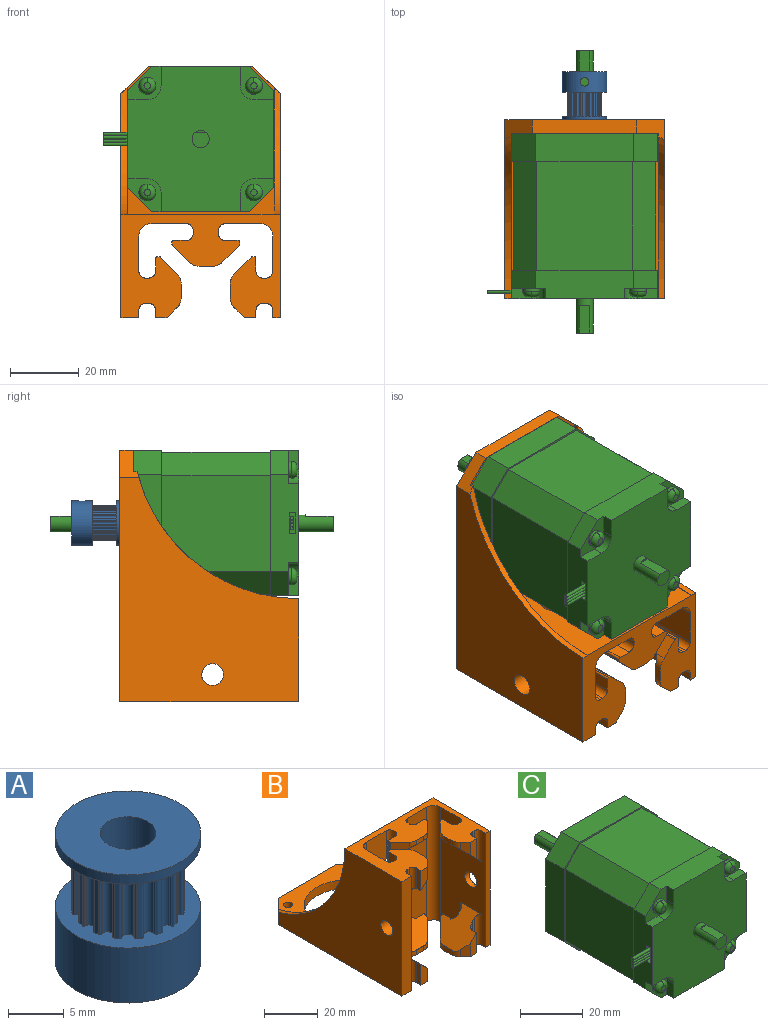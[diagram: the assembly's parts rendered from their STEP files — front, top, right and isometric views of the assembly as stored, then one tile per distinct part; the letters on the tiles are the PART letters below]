
ASSEMBLY  parts=3 mates=2
PART A: 104 faces, bbox 13x13x14 mm
  f0: cylinder r=2.5mm len=14mm, axis (0,0,1), area 214.8mm2, adj f2,f102,f103
  f1: cylinder r=6.5mm len=13mm, axis (0,0,1), area 240.1mm2, adj f2,f3,f103
  f2: plane 13x13mm, normal (0,0,-1), area 113.1mm2, adj f0,f1
  f3: plane 13x13mm, normal (0,0,1), area 62.7mm2, adj f1,f4,f5,f6,f7,f8,f9,f10
  f4: cylinder r=0.15mm len=7mm, axis (0,0,-1), area 1.7mm2, adj f3,f5,f99,f100
  f5: cylinder r=1mm len=7mm, axis (0,0,-1), area 1.7mm2, adj f3,f4,f6,f100
  f6: cylinder r=0.56mm len=7mm, axis (0,0,-1), area 9mm2, adj f3,f5,f7,f100
  f7: cylinder r=1mm len=7mm, axis (0,0,-1), area 1.7mm2, adj f3,f6,f8,f100
  f8: cylinder r=0.15mm len=7mm, axis (0,0,-1), area 1.7mm2, adj f3,f7,f9,f100
  f9: plane 7x0.49mm, normal (0.98,0.2,0), area 3.5mm2, adj f3,f8,f10,f100
  f10: cylinder r=0.15mm len=7mm, axis (0,0,-1), area 1.7mm2, adj f3,f9,f11,f100
  f11: cylinder r=1mm len=7mm, axis (0,0,-1), area 1.7mm2, adj f3,f10,f12,f100
  f12: cylinder r=0.56mm len=7mm, axis (0,0,-1), area 9mm2, adj f3,f11,f13,f100
  f13: cylinder r=1mm len=7mm, axis (0,0,-1), area 1.7mm2, adj f3,f12,f14,f100
  f14: cylinder r=0.15mm len=7mm, axis (0,0,-1), area 1.7mm2, adj f3,f13,f15,f100
  f15: plane 7x0.41mm, normal (0.83,0.56,0), area 3.5mm2, adj f3,f14,f16,f100
  f16: cylinder r=0.15mm len=7mm, axis (0,0,-1), area 1.7mm2, adj f3,f15,f17,f100
  f17: cylinder r=1mm len=7mm, axis (0,0,-1), area 1.7mm2, adj f3,f16,f18,f100
  f18: cylinder r=0.56mm len=7mm, axis (0,0,-1), area 9mm2, adj f3,f17,f19,f100
  f19: cylinder r=1mm len=7mm, axis (0,0,-1), area 1.7mm2, adj f3,f18,f20,f100
  f20: cylinder r=0.15mm len=7mm, axis (0,0,-1), area 1.7mm2, adj f3,f19,f21,f100
  f21: plane 7x0.41mm, normal (0.56,0.83,0), area 3.5mm2, adj f3,f20,f22,f100
  f22: cylinder r=0.15mm len=7mm, axis (0,0,-1), area 1.7mm2, adj f3,f21,f23,f100
  f23: cylinder r=1mm len=7mm, axis (0,0,-1), area 1.7mm2, adj f3,f22,f24,f100
  f24: cylinder r=0.56mm len=7mm, axis (0,0,-1), area 9mm2, adj f3,f23,f25,f100
  f25: cylinder r=1mm len=7mm, axis (0,0,-1), area 1.7mm2, adj f3,f24,f26,f100
  f26: cylinder r=0.15mm len=7mm, axis (0,0,-1), area 1.7mm2, adj f3,f25,f27,f100
  f27: plane 7x0.49mm, normal (0.2,0.98,0), area 3.5mm2, adj f3,f26,f28,f100
  f28: cylinder r=0.15mm len=7mm, axis (0,0,-1), area 1.7mm2, adj f3,f27,f29,f100
  f29: cylinder r=1mm len=7mm, axis (0,0,-1), area 1.7mm2, adj f3,f28,f30,f100
  f30: cylinder r=0.56mm len=7mm, axis (0,0,-1), area 9mm2, adj f3,f29,f31,f100
  f31: cylinder r=1mm len=7mm, axis (0,0,-1), area 1.7mm2, adj f3,f30,f32,f100
  f32: cylinder r=0.15mm len=7mm, axis (0,0,-1), area 1.7mm2, adj f3,f31,f33,f100
  f33: plane 7x0.49mm, normal (-0.2,0.98,0), area 3.5mm2, adj f3,f32,f34,f100
  f34: cylinder r=0.15mm len=7mm, axis (0,0,-1), area 1.7mm2, adj f3,f33,f35,f100
  f35: cylinder r=1mm len=7mm, axis (0,0,-1), area 1.7mm2, adj f3,f34,f36,f100
  f36: cylinder r=0.56mm len=7mm, axis (0,0,-1), area 9mm2, adj f3,f35,f37,f100
  f37: cylinder r=1mm len=7mm, axis (0,0,-1), area 1.7mm2, adj f3,f36,f38,f100
  f38: cylinder r=0.15mm len=7mm, axis (0,0,-1), area 1.7mm2, adj f3,f37,f39,f100
  f39: plane 7x0.41mm, normal (-0.56,0.83,0), area 3.5mm2, adj f3,f38,f40,f100
  f40: cylinder r=0.15mm len=7mm, axis (0,0,-1), area 1.7mm2, adj f3,f39,f41,f100
  f41: cylinder r=1mm len=7mm, axis (0,0,-1), area 1.7mm2, adj f3,f40,f42,f100
  f42: cylinder r=0.56mm len=7mm, axis (0,0,-1), area 9mm2, adj f3,f41,f43,f100
  f43: cylinder r=1mm len=7mm, axis (0,0,-1), area 1.7mm2, adj f3,f42,f44,f100
  f44: cylinder r=0.15mm len=7mm, axis (0,0,-1), area 1.7mm2, adj f3,f43,f45,f100
  f45: plane 7x0.41mm, normal (-0.83,0.56,0), area 3.5mm2, adj f3,f44,f46,f100
  f46: cylinder r=0.15mm len=7mm, axis (0,0,-1), area 1.7mm2, adj f3,f45,f47,f100
  f47: cylinder r=1mm len=7mm, axis (0,0,-1), area 1.7mm2, adj f3,f46,f48,f100
  f48: cylinder r=0.56mm len=7mm, axis (0,0,-1), area 9mm2, adj f3,f47,f49,f100
  f49: cylinder r=1mm len=7mm, axis (0,0,-1), area 1.7mm2, adj f3,f48,f50,f100
  f50: cylinder r=0.15mm len=7mm, axis (0,0,-1), area 1.7mm2, adj f3,f49,f51,f100
  f51: plane 7x0.49mm, normal (-0.98,0.2,0), area 3.5mm2, adj f3,f50,f52,f100
  f52: cylinder r=0.15mm len=7mm, axis (0,0,-1), area 1.7mm2, adj f3,f51,f53,f100
  f53: cylinder r=1mm len=7mm, axis (0,0,-1), area 1.7mm2, adj f3,f52,f54,f100
  f54: cylinder r=0.56mm len=7mm, axis (0,0,-1), area 9mm2, adj f3,f53,f55,f100
  f55: cylinder r=1mm len=7mm, axis (0,0,-1), area 1.7mm2, adj f3,f54,f56,f100
  f56: cylinder r=0.15mm len=7mm, axis (0,0,-1), area 1.7mm2, adj f3,f55,f57,f100
  f57: plane 7x0.49mm, normal (-0.98,-0.2,0), area 3.5mm2, adj f3,f56,f58,f100
  f58: cylinder r=0.15mm len=7mm, axis (0,0,-1), area 1.7mm2, adj f3,f57,f59,f100
  f59: cylinder r=1mm len=7mm, axis (0,0,-1), area 1.7mm2, adj f3,f58,f60,f100
  f60: cylinder r=0.56mm len=7mm, axis (0,0,-1), area 9mm2, adj f3,f59,f61,f100
  f61: cylinder r=1mm len=7mm, axis (0,0,-1), area 1.7mm2, adj f3,f60,f62,f100
  f62: cylinder r=0.15mm len=7mm, axis (0,0,-1), area 1.7mm2, adj f3,f61,f63,f100
  f63: plane 7x0.41mm, normal (-0.83,-0.56,0), area 3.5mm2, adj f3,f62,f64,f100
  f64: cylinder r=0.15mm len=7mm, axis (0,0,-1), area 1.7mm2, adj f3,f63,f65,f100
  f65: cylinder r=1mm len=7mm, axis (0,0,-1), area 1.7mm2, adj f3,f64,f66,f100
  f66: cylinder r=0.56mm len=7mm, axis (0,0,-1), area 9mm2, adj f3,f65,f67,f100
  f67: cylinder r=1mm len=7mm, axis (0,0,-1), area 1.7mm2, adj f3,f66,f68,f100
  f68: cylinder r=0.15mm len=7mm, axis (0,0,-1), area 1.7mm2, adj f3,f67,f69,f100
  f69: plane 7x0.41mm, normal (-0.56,-0.83,0), area 3.5mm2, adj f3,f68,f70,f100
  f70: cylinder r=0.15mm len=7mm, axis (0,0,-1), area 1.7mm2, adj f3,f69,f71,f100
  f71: cylinder r=1mm len=7mm, axis (0,0,-1), area 1.7mm2, adj f3,f70,f72,f100
  f72: cylinder r=0.56mm len=7mm, axis (0,0,-1), area 9mm2, adj f3,f71,f73,f100
  f73: cylinder r=1mm len=7mm, axis (0,0,-1), area 1.7mm2, adj f3,f72,f74,f100
  f74: cylinder r=0.15mm len=7mm, axis (0,0,-1), area 1.7mm2, adj f3,f73,f75,f100
  f75: plane 7x0.49mm, normal (-0.2,-0.98,0), area 3.5mm2, adj f3,f74,f76,f100
  f76: cylinder r=0.15mm len=7mm, axis (0,0,-1), area 1.7mm2, adj f3,f75,f77,f100
  f77: cylinder r=1mm len=7mm, axis (0,0,-1), area 1.7mm2, adj f3,f76,f78,f100
  f78: cylinder r=0.56mm len=7mm, axis (0,0,-1), area 9mm2, adj f3,f77,f79,f100
  f79: cylinder r=1mm len=7mm, axis (0,0,-1), area 1.7mm2, adj f3,f78,f80,f100
  f80: cylinder r=0.15mm len=7mm, axis (0,0,-1), area 1.7mm2, adj f3,f79,f81,f100
  f81: plane 7x0.49mm, normal (0.2,-0.98,0), area 3.5mm2, adj f3,f80,f82,f100
  f82: cylinder r=0.15mm len=7mm, axis (0,0,-1), area 1.7mm2, adj f3,f81,f83,f100
  f83: cylinder r=1mm len=7mm, axis (0,0,-1), area 1.7mm2, adj f3,f82,f84,f100
  f84: cylinder r=0.56mm len=7mm, axis (0,0,-1), area 9mm2, adj f3,f83,f85,f100
  f85: cylinder r=1mm len=7mm, axis (0,0,-1), area 1.7mm2, adj f3,f84,f86,f100
  f86: cylinder r=0.15mm len=7mm, axis (0,0,-1), area 1.7mm2, adj f3,f85,f87,f100
  f87: plane 7x0.41mm, normal (0.56,-0.83,0), area 3.5mm2, adj f3,f86,f88,f100
  f88: cylinder r=0.15mm len=7mm, axis (0,0,-1), area 1.7mm2, adj f3,f87,f89,f100
  f89: cylinder r=1mm len=7mm, axis (0,0,-1), area 1.7mm2, adj f3,f88,f90,f100
  f90: cylinder r=0.56mm len=7mm, axis (0,0,-1), area 9mm2, adj f3,f89,f91,f100
  f91: cylinder r=1mm len=7mm, axis (0,0,-1), area 1.7mm2, adj f3,f90,f92,f100
  f92: cylinder r=0.15mm len=7mm, axis (0,0,-1), area 1.7mm2, adj f3,f91,f93,f100
  f93: plane 7x0.41mm, normal (0.83,-0.56,0), area 3.5mm2, adj f3,f92,f94,f100
  f94: cylinder r=0.15mm len=7mm, axis (0,0,-1), area 1.7mm2, adj f3,f93,f95,f100
  f95: cylinder r=1mm len=7mm, axis (0,0,-1), area 1.7mm2, adj f3,f94,f96,f100
  f96: cylinder r=0.56mm len=7mm, axis (0,0,-1), area 9mm2, adj f3,f95,f97,f100
  f97: cylinder r=1mm len=7mm, axis (0,0,-1), area 1.7mm2, adj f3,f96,f98,f100
  f98: cylinder r=0.15mm len=7mm, axis (0,0,-1), area 1.7mm2, adj f3,f97,f99,f100
  f99: plane 7x0.49mm, normal (0.98,-0.2,0), area 3.5mm2, adj f3,f4,f98,f100
  f100: plane 13x13mm, normal (0,0,-1), area 62.7mm2, adj f4,f5,f6,f7,f8,f9,f10,f11
  f101: cylinder r=6.5mm len=13mm, axis (0,0,-1), area 40.8mm2, adj f100,f102
  f102: plane 13x13mm, normal (0,0,1), area 113.1mm2, adj f0,f101
  f103: cylinder r=1.25mm len=4.34mm, axis (0,-1,0), area 32.2mm2, adj f0,f1
PART B: 154 faces, bbox 46.4x73.1x52.1 mm
  f0: plane 52x10.23mm, normal (0,-1,0), area 397.5mm2, adj f41,f42,f43,f111,f125,f144,f145,f148
  f1: plane 9.14x3.34mm, normal (0,-1,0), area 24.9mm2, adj f91,f101,f111,f137
  f2: plane 9.14x3.34mm, normal (0,-1,0), area 24.9mm2, adj f92,f102,f125,f139
  f3: plane 9.14x3.34mm, normal (0,-1,0), area 24.9mm2, adj f89,f99,f111,f136
  f4: plane 9.14x3.34mm, normal (0,-1,0), area 24.9mm2, adj f90,f100,f125,f141
  f5: cylinder r=1.95mm len=14mm, axis (0,0,-1), area 40.8mm2, adj f7,f111,f117,f138
  f6: cylinder r=1.95mm len=14mm, axis (0,0,-1), area 40.8mm2, adj f8,f117,f125,f140
  f7: plane 12.05x0.96mm, normal (1,0,0), area 11.1mm2, adj f5,f9,f111,f138
  f8: plane 12.05x0.96mm, normal (1,0,0), area 11.1mm2, adj f6,f10,f125,f140
  f9: cylinder r=1.95mm len=11.09mm, axis (0,0,-1), area 30.2mm2, adj f7,f11,f111,f138
  f10: cylinder r=1.95mm len=11.09mm, axis (0,0,-1), area 30.2mm2, adj f8,f12,f125,f140
  f11: plane 9.14x3.77mm, normal (0,1,0), area 34.4mm2, adj f9,f13,f111,f138
  f12: plane 9.14x3.77mm, normal (0,1,0), area 34.4mm2, adj f10,f14,f125,f140
  f13: cylinder r=0.5mm len=9.14mm, axis (0,0,-1), area 7.1mm2, adj f11,f15,f111,f138
  f14: cylinder r=0.5mm len=9.14mm, axis (0,0,-1), area 7.1mm2, adj f12,f16,f125,f140
  f15: plane 8.63x0.53mm, normal (1,0,0), area 4.5mm2, adj f13,f17,f111,f138
  f16: plane 8.63x0.53mm, normal (1,0,0), area 4.5mm2, adj f14,f18,f125,f140
  f17: cylinder r=0.5mm len=8.1mm, axis (0,0,-1), area 3.1mm2, adj f15,f19,f111,f138
  f18: cylinder r=0.5mm len=8.1mm, axis (0,0,-1), area 3.1mm2, adj f16,f20,f125,f140
  f19: plane 7.75x5.05mm, normal (0.71,-0.71,0), area 37.3mm2, adj f17,f21,f111,f138
  f20: plane 7.75x5.05mm, normal (0.71,-0.71,0), area 37.3mm2, adj f18,f22,f125,f140
  f21: cylinder r=4.36mm len=2.78mm, axis (0,0,-1), area 6.5mm2, adj f19,f23,f111,f134,f138
  f22: cylinder r=4.36mm len=2.78mm, axis (0,0,-1), area 6.5mm2, adj f20,f24,f125,f135,f140
  f23: plane 3.8x2mm, normal (0,-1,0), area 7.6mm2, adj f21,f25,f111,f134
  f24: plane 3.8x2mm, normal (0,-1,0), area 7.6mm2, adj f22,f26,f125,f135
  f25: cylinder r=4.36mm len=2.78mm, axis (0,0,-1), area 6.5mm2, adj f23,f27,f111,f134,f138
  f26: cylinder r=4.36mm len=2.78mm, axis (0,0,-1), area 6.5mm2, adj f24,f28,f125,f135,f140
  f27: plane 7.75x5.05mm, normal (-0.71,-0.71,0), area 37.3mm2, adj f25,f29,f111,f138
  f28: plane 7.75x5.05mm, normal (-0.71,-0.71,0), area 37.3mm2, adj f26,f30,f125,f140
  f29: cylinder r=0.5mm len=8.1mm, axis (0,0,-1), area 3.1mm2, adj f27,f31,f111,f138
  f30: cylinder r=0.5mm len=8.1mm, axis (0,0,-1), area 3.1mm2, adj f28,f32,f125,f140
  f31: plane 8.63x0.53mm, normal (-1,0,0), area 4.5mm2, adj f29,f33,f111,f138
  f32: plane 8.63x0.53mm, normal (-1,0,0), area 4.5mm2, adj f30,f34,f125,f140
  f33: cylinder r=0.5mm len=9.14mm, axis (0,0,-1), area 7.1mm2, adj f31,f35,f111,f138
  f34: cylinder r=0.5mm len=9.14mm, axis (0,0,-1), area 7.1mm2, adj f32,f36,f125,f140
  f35: plane 9.14x3.77mm, normal (0,1,0), area 34.4mm2, adj f33,f37,f111,f138
  f36: plane 9.14x3.77mm, normal (0,1,0), area 34.4mm2, adj f34,f38,f125,f140
  f37: cylinder r=1.95mm len=11.09mm, axis (0,0,-1), area 30.2mm2, adj f35,f39,f111,f138
  f38: cylinder r=1.95mm len=11.09mm, axis (0,0,-1), area 30.2mm2, adj f36,f40,f125,f140
  f39: plane 12.05x0.96mm, normal (-1,0,0), area 11.1mm2, adj f37,f41,f111,f138
  f40: plane 11.18x0.96mm, normal (-1,0,0), area 10.7mm2, adj f38,f42,f125,f140,f149
  f41: cylinder r=1.95mm len=13.8mm, axis (0,0,-1), area 38.8mm2, adj f0,f39,f111,f138,f144,f151
  f42: cylinder r=1.95mm len=12.8mm, axis (0,0,-1), area 35.8mm2, adj f0,f40,f125,f145,f149
  f43: cylinder r=3.49mm len=52mm, axis (0,0,-1), area 296.8mm2, adj f0,f111,f118,f125
  f44: cylinder r=1.95mm len=14mm, axis (0,0,-1), area 40.8mm2, adj f46,f111,f118,f136
  f45: cylinder r=1.95mm len=14mm, axis (0,0,-1), area 40.8mm2, adj f47,f118,f125,f141
  f46: plane 12.05x0.96mm, normal (0,1,0), area 11.1mm2, adj f44,f48,f111,f136
  f47: plane 12.05x0.96mm, normal (0,1,0), area 11.1mm2, adj f45,f49,f125,f141
  f48: cylinder r=1.95mm len=11.09mm, axis (0,0,-1), area 30.2mm2, adj f46,f50,f111,f136
  f49: cylinder r=1.95mm len=11.09mm, axis (0,0,-1), area 30.2mm2, adj f47,f51,f125,f141
  f50: plane 9.14x3.77mm, normal (-1,0,0), area 34.4mm2, adj f48,f52,f111,f136
  f51: plane 9.14x3.77mm, normal (-1,0,0), area 34.4mm2, adj f49,f53,f125,f141
  f52: cylinder r=0.5mm len=9.14mm, axis (0,0,-1), area 7.1mm2, adj f50,f54,f111,f136
  f53: cylinder r=0.5mm len=9.14mm, axis (0,0,-1), area 7.1mm2, adj f51,f55,f125,f141
  f54: plane 8.63x0.57mm, normal (0,1,0), area 4.7mm2, adj f52,f56,f111,f136
  f55: plane 8.63x0.57mm, normal (0,1,0), area 4.7mm2, adj f53,f57,f125,f141
  f56: cylinder r=0.5mm len=8.07mm, axis (0,0,-1), area 3.1mm2, adj f54,f58,f111,f136
  f57: cylinder r=0.5mm len=8.07mm, axis (0,0,-1), area 3.1mm2, adj f55,f59,f125,f141
  f58: plane 7.71x5.01mm, normal (0.71,0.71,0), area 36.9mm2, adj f56,f60,f111,f136
  f59: plane 7.71x5.01mm, normal (0.71,0.71,0), area 36.9mm2, adj f57,f61,f125,f141
  f60: cylinder r=4.37mm len=2.79mm, axis (0,0,-1), area 6.5mm2, adj f58,f62,f111,f132,f136
  f61: cylinder r=4.37mm len=2.79mm, axis (0,0,-1), area 6.5mm2, adj f59,f63,f125,f133,f141
  f62: plane 3.87x2mm, normal (1,0,0), area 7.7mm2, adj f60,f64,f111,f132
  f63: plane 3.87x2mm, normal (1,0,0), area 7.7mm2, adj f61,f65,f125,f133
  f64: cylinder r=4.37mm len=3.36mm, axis (0,0,-1), area 8.9mm2, adj f62,f89,f111,f132,f136
  f65: cylinder r=4.37mm len=3.36mm, axis (0,0,-1), area 8.9mm2, adj f63,f90,f125,f133,f141
  f66: cylinder r=4.37mm len=3.36mm, axis (0,0,-1), area 8.9mm2, adj f68,f91,f111,f130,f137
  f67: cylinder r=4.37mm len=3.36mm, axis (0,0,-1), area 8.9mm2, adj f69,f92,f125,f131,f139
  f68: plane 3.87x2mm, normal (-1,0,0), area 7.7mm2, adj f66,f70,f111,f130
  f69: plane 3.87x2mm, normal (-1,0,0), area 7.7mm2, adj f67,f71,f125,f131
  f70: cylinder r=4.37mm len=3.36mm, axis (0,0,-1), area 8.9mm2, adj f68,f72,f111,f130,f137
  f71: cylinder r=4.37mm len=3.36mm, axis (0,0,-1), area 8.9mm2, adj f69,f73,f125,f131,f139
  f72: plane 7.71x4.45mm, normal (-0.71,0.71,0), area 34.5mm2, adj f70,f74,f111,f137
  f73: plane 7.71x4.45mm, normal (-0.71,0.71,0), area 34.5mm2, adj f71,f75,f125,f139
  f74: cylinder r=0.5mm len=8.07mm, axis (0,0,-1), area 3.1mm2, adj f72,f76,f111,f137
  f75: cylinder r=0.5mm len=8.07mm, axis (0,0,-1), area 3.1mm2, adj f73,f77,f125,f139
  f76: plane 8.63x0.57mm, normal (0,1,0), area 4.7mm2, adj f74,f78,f111,f137
  f77: plane 8.63x0.57mm, normal (0,1,0), area 4.7mm2, adj f75,f79,f125,f139
  f78: cylinder r=0.5mm len=9.14mm, axis (0,0,-1), area 7.1mm2, adj f76,f80,f111,f137
  f79: cylinder r=0.5mm len=9.14mm, axis (0,0,-1), area 7.1mm2, adj f77,f81,f125,f139
  f80: plane 9.14x3.77mm, normal (1,0,0), area 34.4mm2, adj f78,f82,f111,f137
  f81: plane 9.14x3.77mm, normal (1,0,0), area 34.4mm2, adj f79,f83,f125,f139
  f82: cylinder r=1.95mm len=11.09mm, axis (0,0,-1), area 30.2mm2, adj f80,f84,f111,f137
  f83: cylinder r=1.95mm len=11.09mm, axis (0,0,-1), area 30.2mm2, adj f81,f85,f125,f139
  f84: plane 12.05x0.96mm, normal (0,1,0), area 11.1mm2, adj f82,f86,f111,f137
  f85: plane 12.05x0.96mm, normal (0,1,0), area 11.1mm2, adj f83,f87,f125,f139
  f86: cylinder r=1.95mm len=14mm, axis (0,0,-1), area 40.8mm2, adj f84,f111,f119,f137
  f87: cylinder r=1.95mm len=14mm, axis (0,0,-1), area 40.8mm2, adj f85,f119,f125,f139
  f88: cylinder r=3.49mm len=52mm, axis (0,0,-1), area 296.8mm2, adj f111,f117,f119,f125
  f89: plane 5.8x2.53mm, normal (0.71,-0.71,0), area 16.2mm2, adj f3,f64,f111,f136
  f90: plane 5.8x2.53mm, normal (0.71,-0.71,0), area 16.2mm2, adj f4,f65,f125,f141
  f91: plane 5.8x2.53mm, normal (-0.71,-0.71,0), area 16.2mm2, adj f1,f66,f111,f137
  f92: plane 5.8x2.53mm, normal (-0.71,-0.71,0), area 16.2mm2, adj f2,f67,f125,f139
  f93: cylinder r=1.95mm len=11.09mm, axis (0,0,-1), area 30.2mm2, adj f95,f99,f111,f136
  f94: cylinder r=1.95mm len=11.09mm, axis (0,0,-1), area 30.2mm2, adj f96,f100,f125,f141
  f95: plane 12.05x0.96mm, normal (0,-1,0), area 11.1mm2, adj f93,f97,f111,f136
  f96: plane 12.05x0.96mm, normal (0,-1,0), area 11.1mm2, adj f94,f98,f125,f141
  f97: cylinder r=1.95mm len=14mm, axis (0,0,-1), area 40.8mm2, adj f95,f111,f118,f136
  f98: cylinder r=1.95mm len=14mm, axis (0,0,-1), area 40.8mm2, adj f96,f118,f125,f141
  f99: plane 9.14x2.21mm, normal (-1,0,0), area 20.2mm2, adj f3,f93,f111,f136
  f100: plane 9.14x2.21mm, normal (-1,0,0), area 20.2mm2, adj f4,f94,f125,f141
  f101: plane 9.14x2.21mm, normal (1,0,0), area 20.2mm2, adj f1,f103,f111,f137
  f102: plane 9.14x2.21mm, normal (1,0,0), area 20.2mm2, adj f2,f104,f125,f139
  f103: cylinder r=1.95mm len=11.09mm, axis (0,0,-1), area 30.2mm2, adj f101,f105,f111,f137
  f104: cylinder r=1.95mm len=11.09mm, axis (0,0,-1), area 30.2mm2, adj f102,f106,f125,f139
  f105: plane 12.05x0.96mm, normal (0,-1,0), area 11.1mm2, adj f103,f107,f111,f137
  f106: plane 12.05x0.96mm, normal (0,-1,0), area 11.1mm2, adj f104,f108,f125,f139
  f107: cylinder r=1.95mm len=14mm, axis (0,0,-1), area 40.8mm2, adj f105,f111,f119,f137
  f108: cylinder r=1.95mm len=14mm, axis (0,0,-1), area 40.8mm2, adj f106,f119,f125,f139
  f109: plane 48x42.7mm, normal (0,1,0), area 1547.3mm2, adj f110,f125,f127,f129,f144,f145,f146,f147
  f110: plane 43.08x42.7mm, normal (0,0,1), area 960.3mm2, adj f109,f115,f120,f121,f122,f123,f124,f127
  f111: plane 73x46.3mm, normal (0,0,-1), area 1851.5mm2, adj f0,f1,f3,f5,f7,f9,f11,f13
  f112: plane 52x2.2mm, normal (0,-1,0), area 114.4mm2, adj f111,f114,f119,f125
  f113: plane 52x5.2mm, normal (0,-1,0), area 270.4mm2, adj f111,f116,f118,f125
  f114: plane 65x52mm, normal (1,0,0), area 2147mm2, adj f111,f112,f125,f126,f143,f152
  f115: plane 30.3x4mm, normal (0,1,0), area 121.2mm2, adj f110,f111,f142,f143
  f116: plane 65x52mm, normal (-1,0,0), area 2147mm2, adj f111,f113,f125,f128,f142,f153
  f117: plane 52x13.06mm, normal (0,-1,0), area 470.1mm2, adj f5,f6,f88,f111,f125,f138,f140,f146
  f118: plane 52x23.67mm, normal (1,0,0), area 884.7mm2, adj f43,f44,f45,f97,f98,f111,f113,f125
  f119: plane 52x23.67mm, normal (-1,0,0), area 884.7mm2, adj f86,f87,f88,f107,f108,f111,f112,f125
  f120: cylinder r=16mm len=32mm, axis (0,0,1), area 402.1mm2, adj f110,f111
  f121: cylinder r=1.7mm len=4mm, axis (0,0,1), area 42.7mm2, adj f110,f111
  f122: cylinder r=1.7mm len=4mm, axis (0,0,1), area 42.7mm2, adj f110,f111
  f123: cylinder r=1.7mm len=4mm, axis (0,0,1), area 42.7mm2, adj f110,f111
  f124: cylinder r=1.7mm len=4mm, axis (0,0,1), area 42.7mm2, adj f110,f111
  f125: plane 46.3x29.92mm, normal (0,0,1), area 761.6mm2, adj f0,f2,f4,f6,f8,f10,f12,f14
  f126: cylinder r=48.28mm len=46.92mm, axis (1,0,0), area 114.1mm2, adj f114,f125,f127,f143
  f127: plane 48x36.88mm, normal (-1,0,0), area 484.7mm2, adj f109,f110,f126,f143
  f128: cylinder r=48.28mm len=46.92mm, axis (-1,0,0), area 114.1mm2, adj f116,f125,f129,f142
  f129: plane 48x36.88mm, normal (1,0,0), area 484.7mm2, adj f109,f110,f128,f142
  f130: plane 7.11x0.31mm, normal (0,0,1), area 1.9mm2, adj f66,f68,f70,f137
  f131: plane 7.11x0.31mm, normal (0,0,-1), area 1.9mm2, adj f67,f69,f71,f139
  f132: plane 7.11x0.31mm, normal (0,0,1), area 1.9mm2, adj f60,f62,f64,f136
  f133: plane 7.11x0.31mm, normal (0,0,-1), area 1.9mm2, adj f61,f63,f65,f141
  f134: plane 7.04x0.31mm, normal (0,0,1), area 1.9mm2, adj f21,f23,f25,f138
  f135: plane 7.04x0.31mm, normal (0,0,-1), area 1.9mm2, adj f22,f24,f26,f140
  f136: plane 17.8x12.09mm, normal (0.71,0,0.71), area 198.9mm2, adj f3,f44,f46,f48,f50,f52,f54,f56
  f137: plane 17.74x12.03mm, normal (-0.71,0,0.71), area 198.9mm2, adj f1,f66,f70,f72,f74,f76,f78,f80
  f138: plane 19.87x12.09mm, normal (0,-0.71,0.71), area 187.4mm2, adj f5,f7,f9,f11,f13,f15,f17,f19
  f139: plane 17.74x12.03mm, normal (-0.71,0,-0.71), area 198.9mm2, adj f2,f67,f71,f73,f75,f77,f79,f81
  f140: plane 19.87x12.09mm, normal (0,-0.71,-0.71), area 177.7mm2, adj f6,f8,f10,f12,f14,f16,f18,f20
  f141: plane 17.8x12.09mm, normal (0.71,0,-0.71), area 198.9mm2, adj f4,f45,f47,f49,f51,f53,f55,f57
  f142: plane 8x8mm, normal (-0.71,0.71,0), area 48.6mm2, adj f110,f111,f115,f116,f128,f129
  f143: plane 8x8mm, normal (0.71,0.71,0), area 48.6mm2, adj f110,f111,f114,f115,f126,f127
  f144: plane 9.82x8.42mm, normal (0.76,0,0.65), area 34.3mm2, adj f0,f41,f109,f148,f151
  f145: plane 9.82x8.42mm, normal (0.76,0,-0.65), area 34.3mm2, adj f0,f42,f109,f148,f149
  f146: plane 9.82x8.41mm, normal (-0.76,0,-0.65), area 35.9mm2, adj f109,f117,f140,f149,f150
  f147: plane 9.82x8.41mm, normal (-0.76,0,0.65), area 34.5mm2, adj f109,f117,f138,f150,f151
  f148: cylinder r=5mm len=6.51mm, axis (0,-1,0), area 18.8mm2, adj f0,f109,f144,f145
  f149: cylinder r=5mm len=7.59mm, axis (0,-1,0), area 42.6mm2, adj f40,f42,f109,f140,f145,f146
  f150: cylinder r=5mm len=6.51mm, axis (0,-1,0), area 18.8mm2, adj f109,f117,f146,f147
  f151: cylinder r=5mm len=7.59mm, axis (0,-1,0), area 36mm2, adj f41,f109,f138,f144,f147
  f152: cylinder r=3.17mm len=6.35mm, axis (-1,0,0), area 43.9mm2, adj f114,f119
  f153: cylinder r=3.17mm len=6.35mm, axis (-1,0,0), area 103.7mm2, adj f116,f118
PART C: 93 faces, bbox 49.3x82x42.3 mm
  f0: plane 42.3x42.3mm, normal (0,1,0), area 858.8mm2, adj f1,f13,f15,f17,f19,f21,f32,f34
  f1: plane 8.25x7mm, normal (0.71,0,0.71), area 81.7mm2, adj f0,f3,f21,f34
  f2: plane 7x7mm, normal (0.71,0,0.71), area 52mm2, adj f12,f22,f23,f35
  f3: plane 42.3x42.3mm, normal (0,-1,0), area 75.6mm2, adj f1,f4,f5,f6,f7,f8,f9,f10
  f4: plane 31.5x6.71mm, normal (0.71,0,0.71), area 298.8mm2, adj f3,f5,f11,f12
  f5: plane 31.5x27.89mm, normal (1,0,0), area 878.4mm2, adj f3,f4,f6,f12
  f6: plane 31.5x6.71mm, normal (0.71,0,-0.71), area 298.8mm2, adj f3,f5,f7,f12
  f7: plane 31.5x27.89mm, normal (0,0,-1), area 878.4mm2, adj f3,f6,f8,f12
  f8: plane 31.5x6.71mm, normal (-0.71,0,-0.71), area 298.8mm2, adj f3,f7,f9,f12
  f9: plane 31.5x27.89mm, normal (-1,0,0), area 878.4mm2, adj f3,f8,f10,f12
  f10: plane 31.5x6.71mm, normal (-0.71,0,0.71), area 298.8mm2, adj f3,f9,f11,f12
  f11: plane 31.5x27.89mm, normal (0,0,1), area 878.4mm2, adj f3,f4,f10,f12
  f12: plane 42.3x42.3mm, normal (0,1,0), area 75.6mm2, adj f2,f4,f5,f6,f7,f8,f9,f10
  f13: plane 28.3x8.25mm, normal (-1,0,0), area 233.5mm2, adj f0,f3,f15,f32
  f14: plane 28.3x8.25mm, normal (-1,0,0), area 207.1mm2, adj f12,f16,f27,f29,f31,f33,f49,f50
  f15: plane 8.25x7mm, normal (-0.71,0,-0.71), area 81.7mm2, adj f0,f3,f13,f17
  f16: plane 7x7mm, normal (-0.71,0,-0.71), area 52mm2, adj f12,f14,f18,f49
  f17: plane 28.3x8.25mm, normal (0,0,-1), area 233.5mm2, adj f0,f3,f15,f19
  f18: plane 28.3x8.25mm, normal (0,0,-1), area 217.6mm2, adj f12,f16,f20,f27,f41,f42,f48,f49
  f19: plane 8.25x7mm, normal (0.71,0,-0.71), area 81.7mm2, adj f0,f3,f17,f21
  f20: plane 7x7mm, normal (0.71,0,-0.71), area 52mm2, adj f12,f18,f22,f41
  f21: plane 28.3x8.25mm, normal (1,0,0), area 233.5mm2, adj f0,f1,f3,f19
  f22: plane 28.3x8.25mm, normal (1,0,0), area 217.6mm2, adj f2,f12,f20,f23,f26,f27,f40,f41
  f23: plane 9.65x9.65mm, normal (0,-1,0), area 46.4mm2, adj f2,f22,f24,f25,f26,f35,f60
  f24: plane 5.65x3mm, normal (1,0,0), area 17mm2, adj f23,f25,f27,f35
  f25: cylinder r=4mm len=4mm, axis (0,1,0), area 18.8mm2, adj f23,f24,f26,f27
  f26: plane 5.65x3mm, normal (0,0,1), area 17mm2, adj f22,f23,f25,f27
  f27: plane 42.3x42.3mm, normal (0,-1,0), area 1410.9mm2, adj f14,f18,f22,f24,f25,f26,f28,f30
  f28: plane 5.65x3mm, normal (-1,0,0), area 17mm2, adj f27,f29,f30,f35
  f29: plane 9.65x9.65mm, normal (0,-1,0), area 46.4mm2, adj f14,f28,f30,f31,f33,f35,f36
  f30: cylinder r=4mm len=4mm, axis (0,-1,0), area 18.8mm2, adj f27,f28,f29,f31
  f31: plane 5.65x3mm, normal (0,0,1), area 17mm2, adj f14,f27,f29,f30
  f32: plane 8.25x7mm, normal (-0.71,0,0.71), area 81.7mm2, adj f0,f3,f13,f34
  f33: plane 7x7mm, normal (-0.71,0,0.71), area 52mm2, adj f12,f14,f29,f35
  f34: plane 28.3x8.25mm, normal (0,0,1), area 233.5mm2, adj f0,f1,f3,f32
  f35: plane 28.3x8.25mm, normal (0,0,1), area 217.6mm2, adj f2,f12,f23,f24,f27,f28,f29,f33
  f36: cylinder r=2.45mm len=4.9mm, axis (0,-1,0), area 15.4mm2, adj f29,f37,f39
  f37: torus R=0.95mm, axis (0,-1,0), area 14.1mm2, adj f36,f38,f39
  f38: plane 1.9x1.9mm, normal (0,-1,0), area 2.8mm2, adj f37,f39
  f39: torus R=0.95mm, axis (0,-1,0), area 14.1mm2, adj f36,f37,f38
  f40: plane 5.65x3mm, normal (0,0,-1), area 17mm2, adj f22,f27,f41,f43
  f41: plane 9.65x9.65mm, normal (0,-1,0), area 46.4mm2, adj f18,f20,f22,f40,f42,f43,f44
  f42: plane 5.65x3mm, normal (1,0,0), area 17mm2, adj f18,f27,f41,f43
  f43: cylinder r=4mm len=4mm, axis (0,-1,0), area 18.8mm2, adj f27,f40,f41,f42
  f44: cylinder r=2.45mm len=4.9mm, axis (0,-1,0), area 15.4mm2, adj f41,f45,f47
  f45: torus R=0.95mm, axis (0,-1,0), area 14.1mm2, adj f44,f46,f47
  f46: plane 1.9x1.9mm, normal (0,-1,0), area 2.8mm2, adj f45,f47
  f47: torus R=0.95mm, axis (0,-1,0), area 14.1mm2, adj f44,f45,f46
  f48: plane 5.65x3mm, normal (-1,0,0), area 17mm2, adj f18,f27,f49,f51
  f49: plane 9.65x9.65mm, normal (0,-1,0), area 46.4mm2, adj f14,f16,f18,f48,f50,f51,f52
  f50: plane 5.65x3mm, normal (0,0,-1), area 17mm2, adj f14,f27,f49,f51
  f51: cylinder r=4mm len=4mm, axis (0,1,0), area 18.8mm2, adj f27,f48,f49,f50
  f52: cylinder r=2.45mm len=4.9mm, axis (0,1,0), area 15.4mm2, adj f49,f53,f55
  f53: torus R=0.95mm, axis (0,1,0), area 14.1mm2, adj f52,f54,f55
  f54: plane 1.9x1.9mm, normal (0,-1,0), area 2.8mm2, adj f53,f55
  f55: torus R=0.95mm, axis (0,1,0), area 14.1mm2, adj f52,f53,f54
  f56: cylinder r=2.5mm len=10mm, axis (0,-1,0), area 131.3mm2, adj f27,f57,f58,f59
  f57: plane 8x3mm, normal (0,0,1), area 24mm2, adj f56,f58,f59
  f58: plane 5x4.5mm, normal (0,-1,0), area 18.6mm2, adj f56,f57
  f59: plane 3x0.5mm, normal (0,-1,0), area 1mm2, adj f56,f57
  f60: cylinder r=2.45mm len=4.9mm, axis (0,1,0), area 15.4mm2, adj f23,f61,f63
  f61: torus R=0.95mm, axis (0,1,0), area 14.1mm2, adj f60,f62,f63
  f62: plane 1.9x1.9mm, normal (0,-1,0), area 2.8mm2, adj f61,f63
  f63: torus R=0.95mm, axis (0,1,0), area 14.1mm2, adj f60,f61,f62
  f64: plane 3x1.75mm, normal (0,0,1), area 5.3mm2, adj f14,f65,f67,f68
  f65: plane 6x3mm, normal (0,-1,0), area 18mm2, adj f14,f64,f66,f68
  f66: plane 3x1.75mm, normal (0,0,-1), area 5.3mm2, adj f14,f65,f67,f68
  f67: plane 6x3mm, normal (0,1,0), area 18mm2, adj f14,f64,f66,f68
  f68: plane 6x1.75mm, normal (-1,0,0), area 7.6mm2, adj f64,f65,f66,f67,f69,f71,f73,f75
  f69: cylinder r=0.48mm len=10mm, axis (-1,0,0), area 30mm2, adj f68,f70
  f70: plane 0.96x0.96mm, normal (-1,0,0), area 0.7mm2, adj f69
  f71: cylinder r=0.48mm len=10mm, axis (-1,0,0), area 30mm2, adj f68,f72
  f72: plane 0.96x0.96mm, normal (-1,0,0), area 0.7mm2, adj f71
  f73: cylinder r=0.48mm len=10mm, axis (-1,0,0), area 30mm2, adj f68,f74
  f74: plane 0.96x0.96mm, normal (-1,0,0), area 0.7mm2, adj f73
  f75: cylinder r=0.48mm len=10mm, axis (-1,0,0), area 30mm2, adj f68,f76
  f76: plane 0.96x0.96mm, normal (-1,0,0), area 0.7mm2, adj f75
  f77: cylinder r=1.5mm len=4.5mm, axis (0,-1,0), area 42.4mm2, adj f0,f78
  f78: plane 3x3mm, normal (0,1,0), area 7.1mm2, adj f77
  f79: cylinder r=1.5mm len=4.5mm, axis (0,1,0), area 42.4mm2, adj f0,f80
  f80: plane 3x3mm, normal (0,1,0), area 7.1mm2, adj f79
  f81: cylinder r=1.5mm len=4.5mm, axis (0,1,0), area 42.4mm2, adj f0,f82
  f82: plane 3x3mm, normal (0,1,0), area 7.1mm2, adj f81
  f83: cylinder r=1.5mm len=4.5mm, axis (0,-1,0), area 42.4mm2, adj f0,f84
  f84: plane 3x3mm, normal (0,1,0), area 7.1mm2, adj f83
  f85: cylinder r=16mm len=32mm, axis (0,1,0), area 40.2mm2, adj f0,f86
  f86: plane 32x32mm, normal (0,1,0), area 424.1mm2, adj f85,f87
  f87: cylinder r=11mm len=22mm, axis (0,1,0), area 165.9mm2, adj f86,f88
  f88: plane 22x22mm, normal (0,1,0), area 360.5mm2, adj f87,f89
  f89: cylinder r=2.5mm len=22mm, axis (0,1,0), area 297.3mm2, adj f88,f90,f91,f92
  f90: plane 3x0.5mm, normal (0,1,0), area 1mm2, adj f89,f91
  f91: plane 15x3mm, normal (0,0,1), area 45mm2, adj f89,f90,f92
  f92: plane 5x4.5mm, normal (0,1,0), area 18.6mm2, adj f89,f91
PLACE A rot(axis=(1,0,0),90deg) t=(-31.56,23.26,0.34)mm
PLACE B rot(axis=(1,0,0),90deg) t=(-31.56,15.26,-2.66)mm
PLACE C t=(-31.56,11.26,0.34)mm fixed
MATE revolute A.f0 <-> C.f56  axis (0,1,0) through (-31.56,29.26,0.34)mm
MATE fastened C.f56 <-> B.f120  axis (0,1,0) through (-31.56,11.26,0.34)mm
